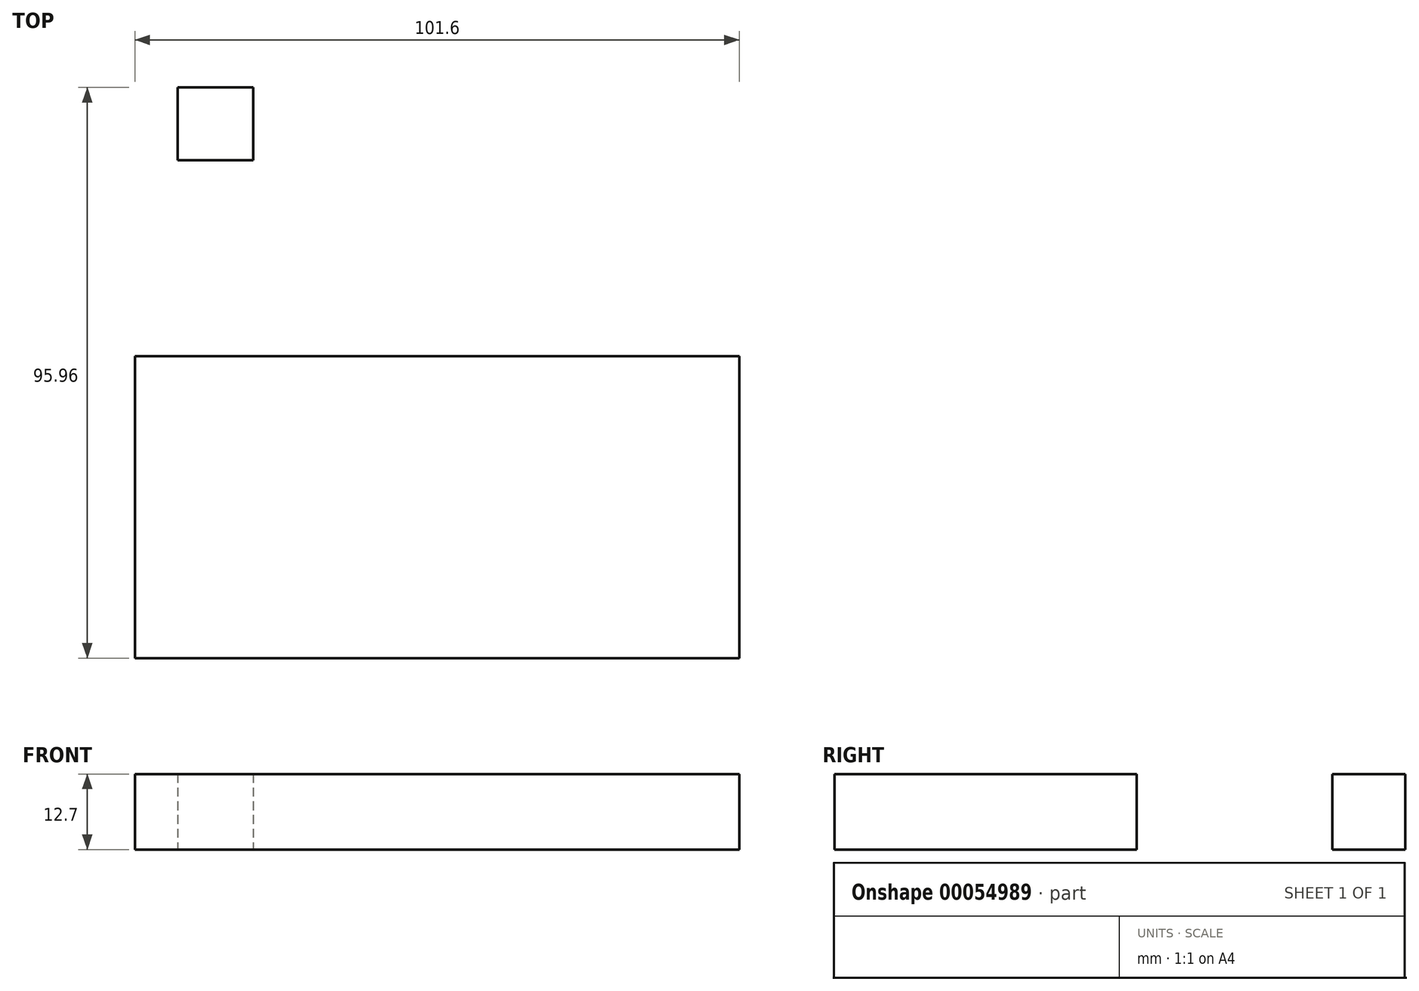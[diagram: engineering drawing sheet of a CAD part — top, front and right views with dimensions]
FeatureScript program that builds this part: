
annotation { "Feature Type Name" : "Feature", "Feature Type Description" : "" }
export const myFeature = defineFeature(function(context is Context, id is Id, definition is map)
    precondition{}
    {
        {
            var Q0;
            Q0=qCreatedBy(makeId("Top.planeOp"),FACE);
            var sketch = newSketch(context, id + "F0", { "sketchPlane" : qUnion([Q0])});
            skLineSegment(sketch, "E0.bottom", {"start": v(-49.52, -24.7) * mm, "end": v(52.08, -24.7) * mm});
            skLineSegment(sketch, "E0.top", {"start": v(-49.52, 26.1) * mm, "end": v(52.08, 26.1) * mm});
            skLineSegment(sketch, "E0.left", {"start": v(-49.52, -24.7) * mm, "end": v(-49.52, 26.1) * mm});
            skLineSegment(sketch, "E0.right", {"start": v(52.08, -24.7) * mm, "end": v(52.08, 26.1) * mm});
            skLineSegment(sketch, "E1.bottom", {"start": v(-42.3, 59.04) * mm, "end": v(-29.6, 59.04) * mm});
            skLineSegment(sketch, "E1.top", {"start": v(-42.3, 71.27) * mm, "end": v(-29.6, 71.27) * mm});
            skLineSegment(sketch, "E1.left", {"start": v(-42.3, 59.04) * mm, "end": v(-42.3, 71.27) * mm});
            skLineSegment(sketch, "E1.right", {"start": v(-29.6, 59.04) * mm, "end": v(-29.6, 71.27) * mm});
            skLineSegment(sketch, "E2.bottom", {"start": v(-9.38, 52.45) * mm, "end": v(3.32, 52.45) * mm});
            skLineSegment(sketch, "E2.top", {"start": v(-9.38, 65.15) * mm, "end": v(3.32, 65.15) * mm});
            skLineSegment(sketch, "E2.left", {"start": v(-9.38, 52.45) * mm, "end": v(-9.38, 65.15) * mm});
            skLineSegment(sketch, "E2.right", {"start": v(3.32, 52.45) * mm, "end": v(3.32, 65.15) * mm});
            skSolve(sketch);
        }
        {
            var Q0;
            Q0=makeQuery(id+"F0.imprint","IMPRINT",FACE,{"disambiguationData":[TD([[makeQuery(id+"F0.imprint","IMPRINT",EDGE,{"derivedFrom":sQuery(id+"F0.wireOp",EDGE,"E0.bottom")}),1.0]])]});
            extrude(context, id + "F1", {"entities" : qUnion([Q0]), "depth" : 12.7 * mm});
        }
        {
            var Q0;
            Q0 = qSketchRegion(id + "F0", true);
            extrude(context, id + "F2", {"entities" : qUnion([Q0]), "operationType" : NewBodyOperationType.ADD, "depth" : 12.7 * mm});
        }
        {
            var Q0;
            Q0=makeQuery(id+"F2.opExtrude","SWEPT_BODY",BODY,{"disambiguationData":[OSD([sQuery(id+"F0.wireOp",EDGE,"E2.bottom"),sQuery(id+"F0.wireOp",EDGE,"E2.top"),sQuery(id+"F0.wireOp",EDGE,"E2.left"),sQuery(id+"F0.wireOp",EDGE,"E2.right")])]});
            deleteBodies(context, id + "F3", {"entities" : qUnion([Q0])});
        }
    });
